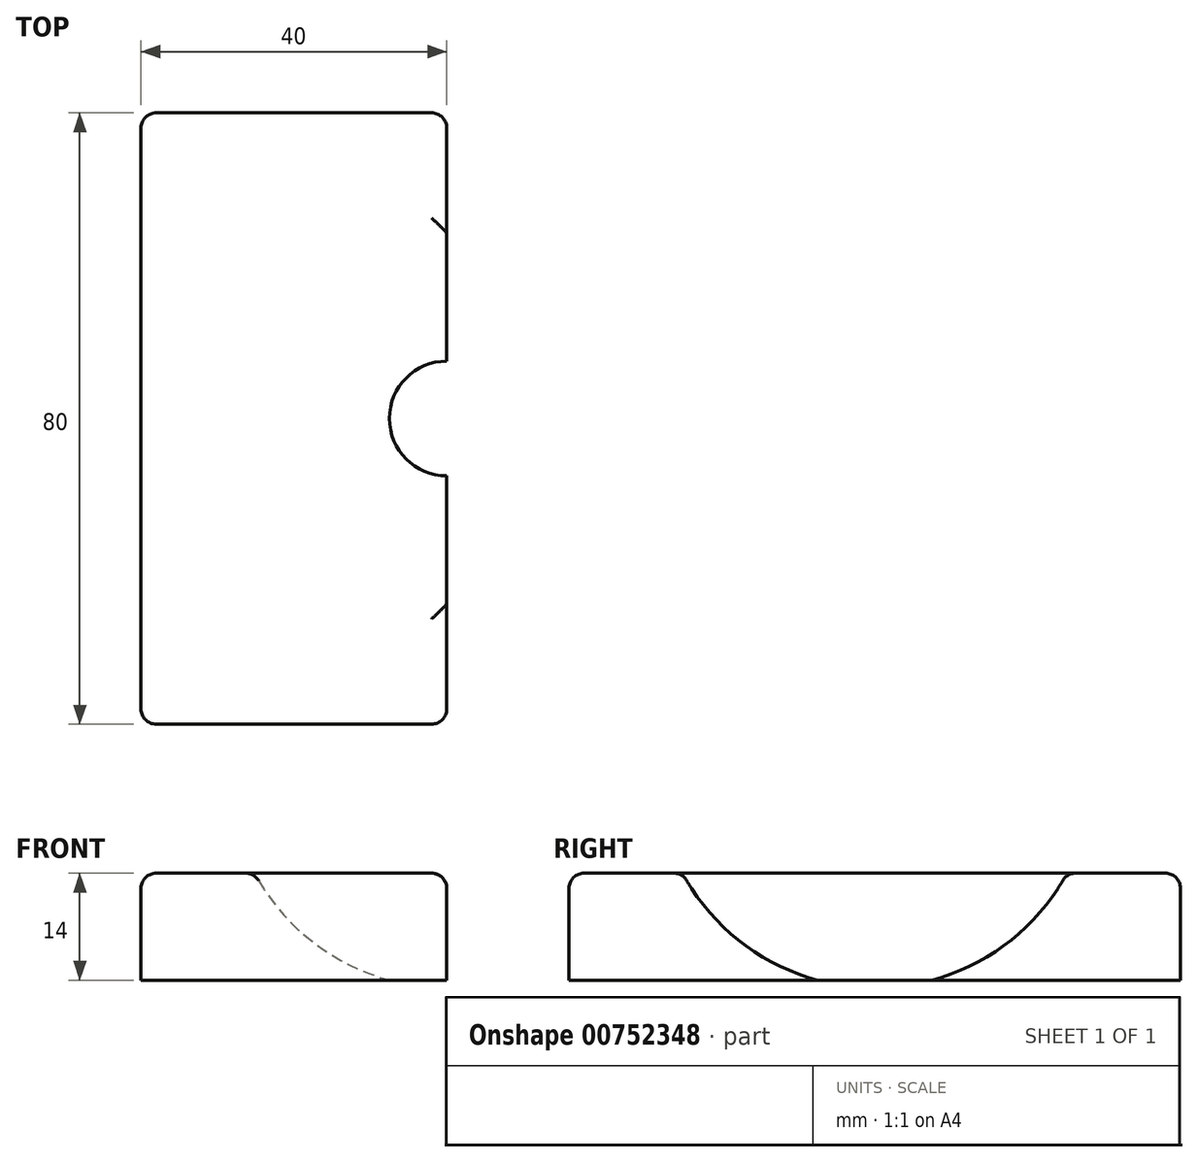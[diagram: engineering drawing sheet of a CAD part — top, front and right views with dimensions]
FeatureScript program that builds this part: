
annotation { "Feature Type Name" : "Feature", "Feature Type Description" : "" }
export const myFeature = defineFeature(function(context is Context, id is Id, definition is map)
    precondition{}
    {
        {
            var Q0;
            Q0=qCreatedBy(makeId("Top.planeOp"),FACE);
            var sketch = newSketch(context, id + "F0", { "sketchPlane" : qUnion([Q0])});
            skLineSegment(sketch, "E0.bottom", {"start": v(0, 0) * mm, "end": v(40, 0) * mm});
            skLineSegment(sketch, "E0.top", {"start": v(0, -80) * mm, "end": v(40, -80) * mm});
            skLineSegment(sketch, "E0.left", {"start": v(0, 0) * mm, "end": v(0, -80) * mm});
            skLineSegment(sketch, "E0.right", {"start": v(40, 0) * mm, "end": v(40, -80) * mm});
            skSolve(sketch);
        }
        {
            var Q0;
            Q0=makeQuery(id+"F0.imprint","IMPRINT",FACE,{"disambiguationData":[TD([[makeQuery(id+"F0.imprint","IMPRINT",EDGE,{"derivedFrom":sQuery(id+"F0.wireOp",EDGE,"E0.bottom")}),-1.0]])]});
            extrude(context, id + "F1", {"entities" : qUnion([Q0]), "depth" : 14 * mm, "offsetDistance" : 25 * mm});
        }
        {
            var Q0;
            Q0=makeQuery(id+"F1.opExtrude","SWEPT_FACE",FACE,{"disambiguationData":[OSD([sQuery(id+"F0.wireOp",EDGE,"E0.right")])]});
            var sketch = newSketch(context, id + "F2", { "sketchPlane" : qUnion([Q0])});
            skArc(sketch, "E1", {"start": v(-40, -1) * mm, "mid": v(-11.4, 27.6) * mm, "end": v(-40, 56.2) * mm});
            skLineSegment(sketch, "E2", {"start": v(-40, 56.2) * mm, "end": v(-40, -1) * mm});
            skPoint(sketch, "E3.0", {"position": v(-40, 0) * mm});
            skSolve(sketch);
        }
        {
            var Q0;
            {var subQ0=sQuery(id+"F2.wireOp",EDGE,"E1");var subQ1=sQuery(id+"F0.wireOp",EDGE,"E0.right");var subQ2=makeQuery(id+"F1.opExtrude","CAP_EDGE",EDGE,{"disambiguationData":[OSD([subQ1])],"isStart":true});var subQ3=makeQuery(id+"F2.imprint","INTERSECT",VERTEX,{"derivedFrom":[subQ2,subQ0]});Q0=makeQuery(id+"F2.imprint","IMPRINT",FACE,{"disambiguationData":[TD([[makeQuery(id+"F2.imprint","IMPRINT",EDGE,{"disambiguationData":[TD([[subQ3,-1.0]])],"derivedFrom":subQ0}),1.0]])]});}
            var Q1;
            {var subQ0=sQuery(id+"F2.wireOp",EDGE,"E2");var subQ1=sQuery(id+"F2.wireOp",EDGE,"E1");var subQ2=makeQuery(id+"F2.imprint","INTERSECT",VERTEX,{"disambiguationData":[OD(1.0)],"derivedFrom":[subQ1,subQ0]});Q1=makeQuery(id+"F2.imprint","IMPRINT",FACE,{"disambiguationData":[TD([[makeQuery(id+"F2.imprint","IMPRINT",EDGE,{"disambiguationData":[TD([[subQ2,1.0]])],"derivedFrom":subQ1}),1.0]])]});}
            var Q2;
            {var subQ0=sQuery(id+"F2.wireOp",EDGE,"E2");var subQ1=sQuery(id+"F2.wireOp",EDGE,"E1");var subQ2=makeQuery(id+"F2.imprint","INTERSECT",VERTEX,{"disambiguationData":[OD(0.0)],"derivedFrom":[subQ1,subQ0]});Q2=makeQuery(id+"F2.imprint","IMPRINT",FACE,{"disambiguationData":[TD([[makeQuery(id+"F2.imprint","IMPRINT",EDGE,{"disambiguationData":[TD([[subQ2,-1.0]])],"derivedFrom":subQ1}),1.0]])]});}
            var Q3;
            Q3=sQuery(id+"F2.wireOp",EDGE,"E2");
            revolve(context, id + "F3", {"operationType" : NewBodyOperationType.REMOVE, "surfaceOperationType" : NewSurfaceOperationType.NEW, "entities" : qUnion([Q0, Q1, Q2]), "axis" : qUnion([Q3]), "revolveType" : RevolveType.FULL, "oppositeDirection" : true});
        }
        {
            var Q0;
            Q0=makeQuery(id+"F1.opExtrude","CAP_FACE",FACE,{"disambiguationData":[OSD([sQuery(id+"F0.wireOp",EDGE,"E0.bottom"),sQuery(id+"F0.wireOp",EDGE,"E0.top"),sQuery(id+"F0.wireOp",EDGE,"E0.left"),sQuery(id+"F0.wireOp",EDGE,"E0.right")])],"isStart":false});
            var Q1;
            Q1=makeQuery(id+"F1.opExtrude","SWEPT_EDGE",EDGE,{"disambiguationData":[OSD([sQuery(id+"F0.wireOp",EDGE,"E0.top"),sQuery(id+"F0.wireOp",EDGE,"E0.right")])]});
            var Q2;
            Q2=makeQuery(id+"F1.opExtrude","SWEPT_EDGE",EDGE,{"disambiguationData":[OSD([sQuery(id+"F0.wireOp",EDGE,"E0.top"),sQuery(id+"F0.wireOp",EDGE,"E0.left")])]});
            var Q3;
            Q3=makeQuery(id+"F1.opExtrude","SWEPT_EDGE",EDGE,{"disambiguationData":[OSD([sQuery(id+"F0.wireOp",EDGE,"E0.bottom"),sQuery(id+"F0.wireOp",EDGE,"E0.right")])]});
            var Q4;
            Q4=makeQuery(id+"F1.opExtrude","SWEPT_EDGE",EDGE,{"disambiguationData":[OSD([sQuery(id+"F0.wireOp",EDGE,"E0.bottom"),sQuery(id+"F0.wireOp",EDGE,"E0.left")])]});
            fillet(context, id + "F4", {"entities" : qUnion([Q0, Q1, Q2, Q3, Q4]), "radius" : 2 * mm, "tangentPropagation" : true, "allowEdgeOverflow" : false});
        }
    });
